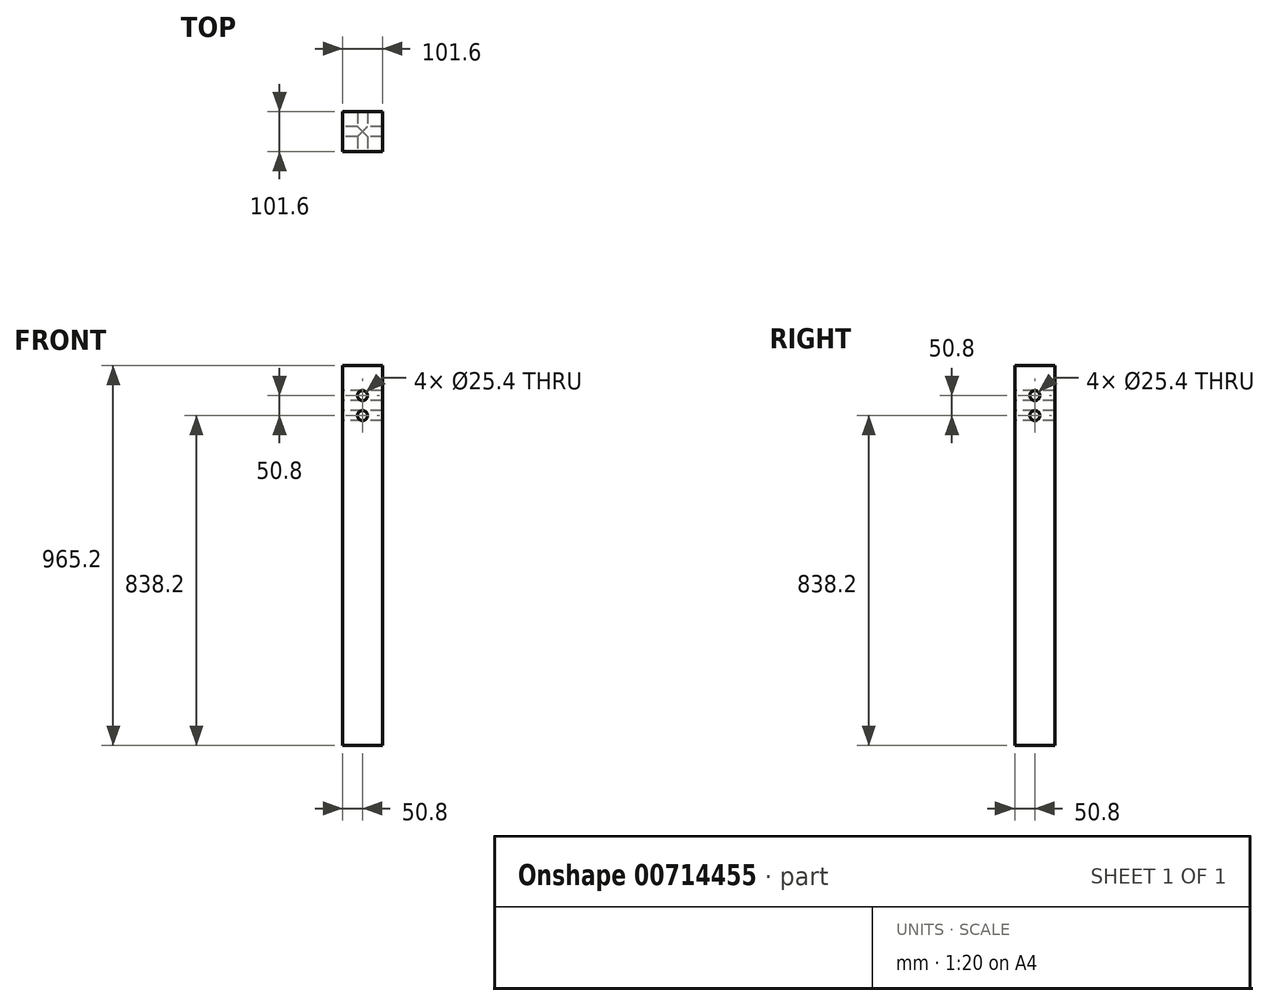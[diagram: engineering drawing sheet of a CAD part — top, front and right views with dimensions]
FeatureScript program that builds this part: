
annotation { "Feature Type Name" : "Feature", "Feature Type Description" : "" }
export const myFeature = defineFeature(function(context is Context, id is Id, definition is map)
    precondition{}
    {
        {
            var Q0;
            Q0=qCreatedBy(makeId("Front.planeOp"),FACE);
            var sketch = newSketch(context, id + "F0", { "sketchPlane" : qUnion([Q0])});
            skLineSegment(sketch, "E0.bottom", {"start": v(0, 965.2) * mm, "end": v(101.6, 965.2) * mm});
            skLineSegment(sketch, "E0.top", {"start": v(0, 0) * mm, "end": v(101.6, 0) * mm});
            skLineSegment(sketch, "E0.left", {"start": v(0, 965.2) * mm, "end": v(0, 0) * mm});
            skLineSegment(sketch, "E0.right", {"start": v(101.6, 965.2) * mm, "end": v(101.6, 0) * mm});
            skSolve(sketch);
        }
        {
            var Q0;
            Q0 = qSketchRegion(id + "F0", true);
            extrude(context, id + "F1", {"entities" : qUnion([Q0]), "depth" : 101.6 * mm, "offsetDistance" : 25.4 * mm});
        }
        {
            var Q0;
            Q0=makeQuery(id+"F1.opExtrude","CAP_FACE",FACE,{"disambiguationData":[OSD([sQuery(id+"F0.wireOp",EDGE,"E0.bottom"),sQuery(id+"F0.wireOp",EDGE,"E0.top"),sQuery(id+"F0.wireOp",EDGE,"E0.left"),sQuery(id+"F0.wireOp",EDGE,"E0.right")])],"isStart":false});
            var sketch = newSketch(context, id + "F2", { "sketchPlane" : qUnion([Q0])});
            skLineSegment(sketch, "E1", {"start": v(50.8, 965.2) * mm, "end": v(50.8, 914.4) * mm, "construction": true});
            skLineSegment(sketch, "E2", {"start": v(50.8, 914.4) * mm, "end": v(50.8, 863.6) * mm});
            skLineSegment(sketch, "E3", {"start": v(50.8, 863.6) * mm, "end": v(50.8, 812.8) * mm});
            skPoint(sketch, "E4", {"position": v(50.8, 838.2) * mm});
            skPoint(sketch, "E5", {"position": v(50.8, 889) * mm});
            skCircle(sketch, "E6", {"center": v(50.8, 838.2) * mm, "radius": 12.7 * mm});
            skCircle(sketch, "E7", {"center": v(50.8, 889) * mm, "radius": 12.7 * mm});
            skSolve(sketch);
        }
        {
            var Q0;
            Q0 = qSketchRegion(id + "F2", true);
            extrude(context, id + "F3", {"entities" : qUnion([Q0]), "operationType" : NewBodyOperationType.REMOVE, "endBound" : BoundingType.THROUGH_ALL, "oppositeDirection" : true, "depth" : 25.4 * mm, "offsetDistance" : 25.4 * mm});
        }
        {
            var Q0;
            Q0=makeQuery(id+"F1.opExtrude","SWEPT_FACE",FACE,{"disambiguationData":[OSD([sQuery(id+"F0.wireOp",EDGE,"E0.left")])]});
            var sketch = newSketch(context, id + "F4", { "sketchPlane" : qUnion([Q0])});
            skLineSegment(sketch, "E8", {"start": v(50.8, 965.2) * mm, "end": v(50.8, 914.4) * mm, "construction": true});
            skLineSegment(sketch, "E9", {"start": v(50.8, 914.4) * mm, "end": v(50.8, 863.6) * mm});
            skLineSegment(sketch, "E10", {"start": v(50.8, 863.6) * mm, "end": v(50.8, 812.8) * mm});
            skPoint(sketch, "E11", {"position": v(50.8, 838.2) * mm});
            skPoint(sketch, "E12", {"position": v(50.8, 889) * mm});
            skCircle(sketch, "E13", {"center": v(50.8, 838.2) * mm, "radius": 12.7 * mm});
            skCircle(sketch, "E14", {"center": v(50.8, 889) * mm, "radius": 12.7 * mm});
            skSolve(sketch);
        }
        {
            var Q0;
            Q0 = qSketchRegion(id + "F4", true);
            extrude(context, id + "F5", {"entities" : qUnion([Q0]), "operationType" : NewBodyOperationType.REMOVE, "endBound" : BoundingType.THROUGH_ALL, "oppositeDirection" : true, "depth" : 25.4 * mm, "offsetDistance" : 25.4 * mm});
        }
    });
